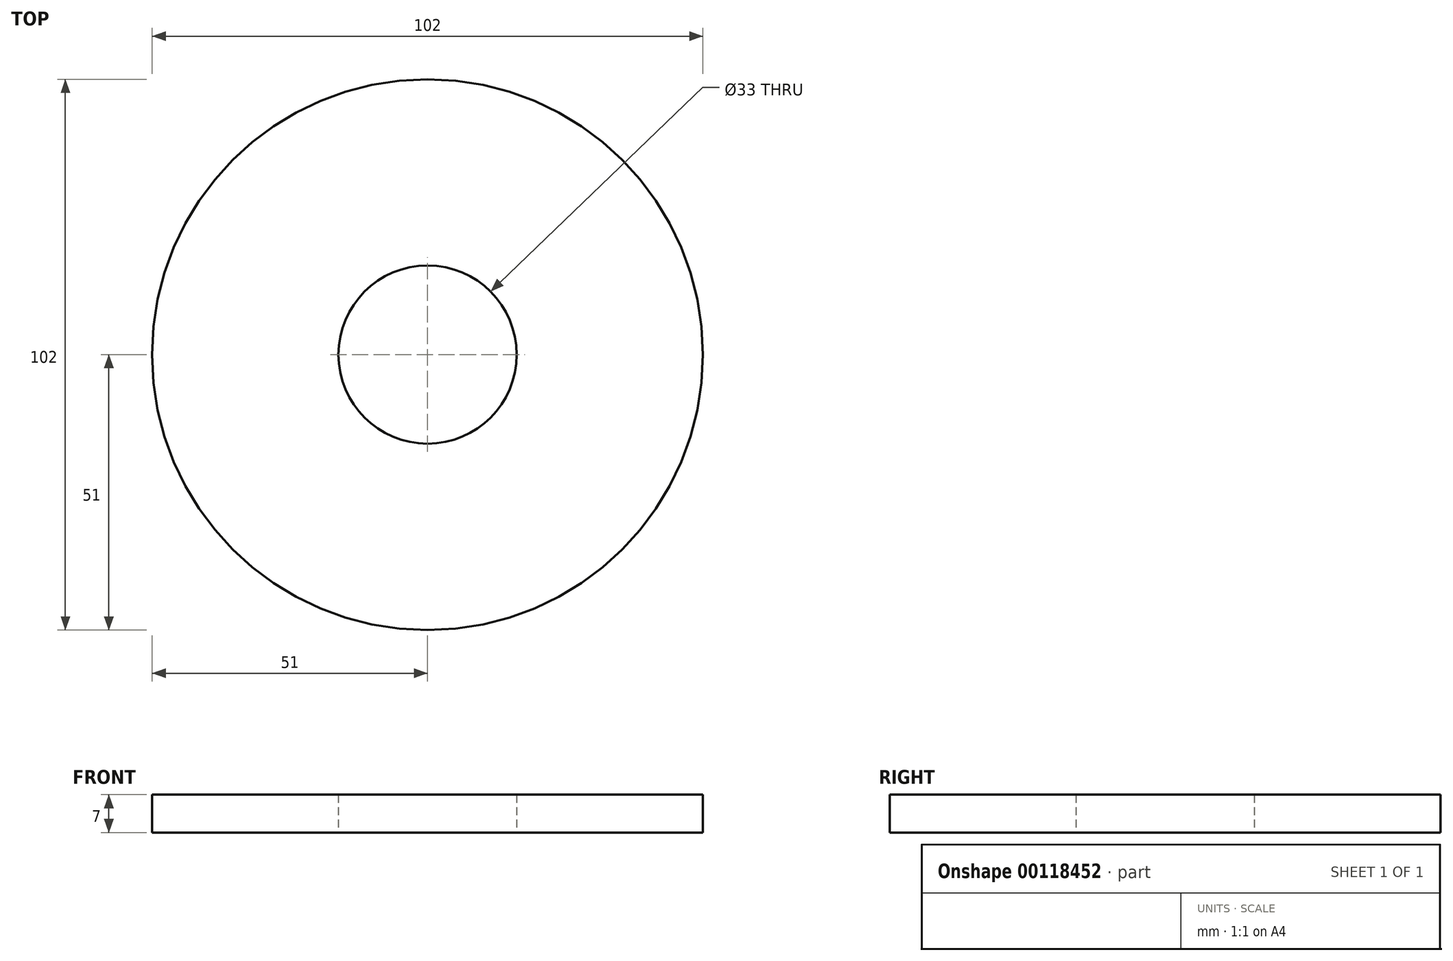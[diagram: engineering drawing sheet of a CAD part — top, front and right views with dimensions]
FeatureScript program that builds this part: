
annotation { "Feature Type Name" : "Feature", "Feature Type Description" : "" }
export const myFeature = defineFeature(function(context is Context, id is Id, definition is map)
    precondition{}
    {
        {
            var Q0;
            Q0=qCreatedBy(makeId("Top.planeOp"),FACE);
            var sketch = newSketch(context, id + "F0", { "sketchPlane" : qUnion([Q0])});
            skCircle(sketch, "E0", {"center": v(0, 0) * mm, "radius": 16.5 * mm});
            skCircle(sketch, "E1", {"center": v(0, 0) * mm, "radius": 51 * mm});
            skSolve(sketch);
        }
        {
            var Q0;
            Q0 = qSketchRegion(id + "F0", true);
            extrude(context, id + "F1", {"entities" : qUnion([Q0]), "depth" : 7 * mm});
        }
    });
